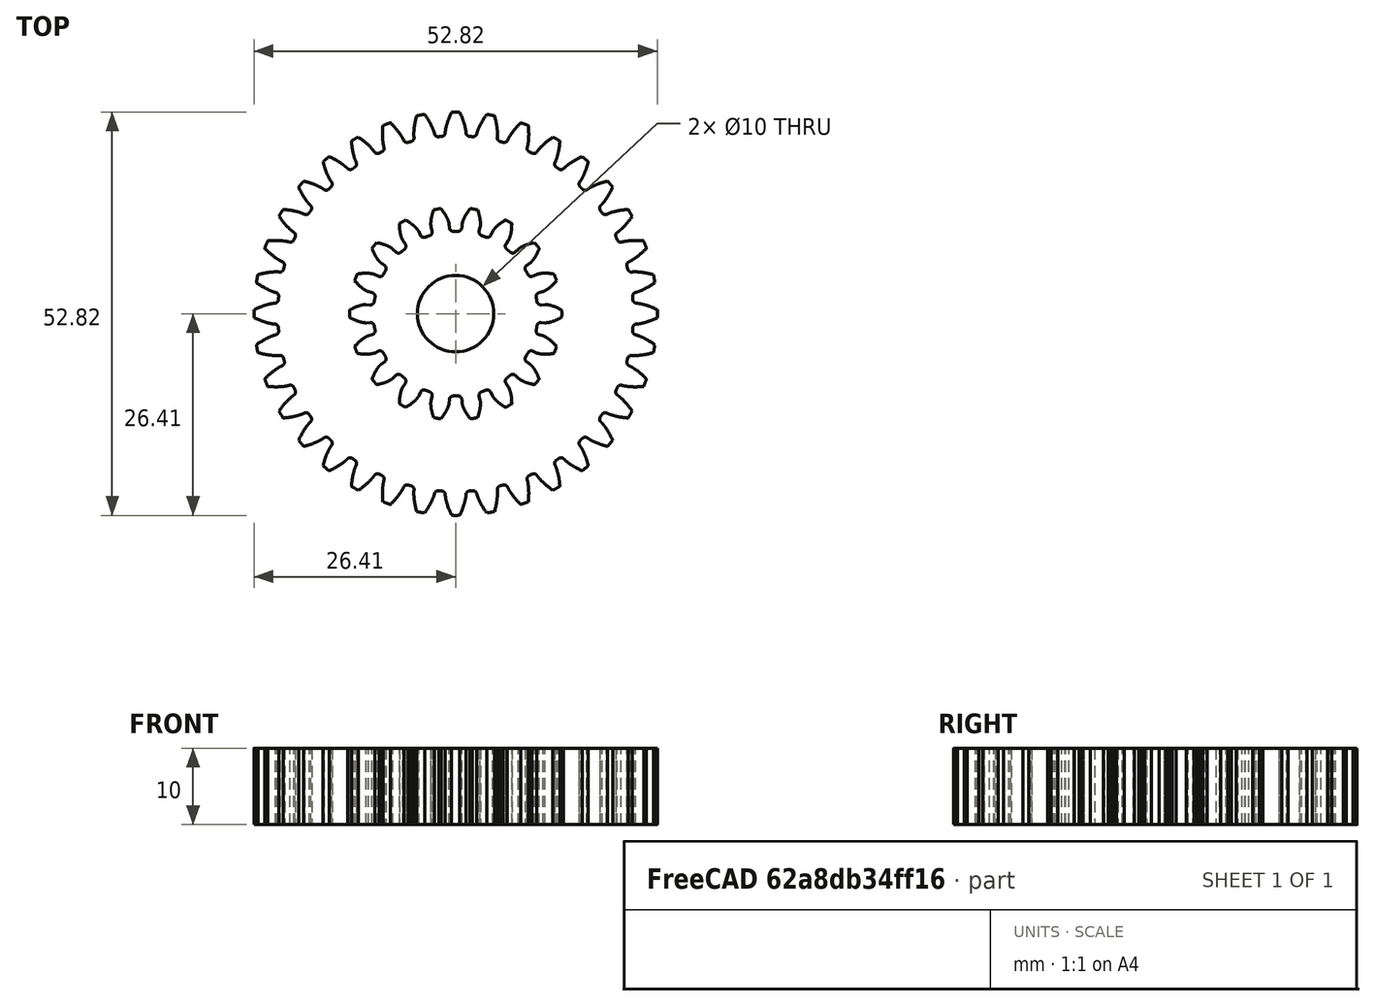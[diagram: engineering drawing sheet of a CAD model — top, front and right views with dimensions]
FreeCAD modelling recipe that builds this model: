
FCSTD DOCUMENT  (FreeCAD 2023.521R36908 (Git))
Label: spur-gear
License: All rights reserved
objects: Part::Part2DObjectPython×2, PartDesign::Pad×2, PartDesign::Body×2, Part::Cylinder×2, Part::Cut×2, App::Part×2
note: 14 computed .brp shape members not serialized (recipe doc carries the construction recipe); baked Part::Feature solids carry a one-line shape summary decoded from their .brp

FEATURE [Part::Part2DObjectPython] InvoluteGear  # Draft 2D object (typed FeaturePython)
  ExternalGear = true
  HighPrecision = true
  InvalidShape = false
  Modules = 1.39
  NumberOfTeeth = 36
  PressureAngle = 20
  TreeRank = 14
  ValidateShape = false
FEATURE [PartDesign::Pad] Pad
  AddSubType = 0
  AlongSketchNormal = false
  AutoTaperInnerAngle = true
  CheckUpToFaceLimits = true
  ClaimChildren = false
  Direction = (0,0,1)
  Fit = 0
  FitJoin = 0
  InnerFit = 0
  InnerFitJoin = 0
  InvalidShape = false
  Length = 10
  Length2 = 10
  Linearize = true
  NewSolid = false
  Profile = -> InvoluteGear
  ReferenceAxis = -> InvoluteGear [N_Axis]
  Suppress = false
  TaperInnerAngle = 0
  TaperInnerAngleRev = 0
  TreeRank = 15
  Type = 0
  ValidateShape = true
  _ProfileBasedVersion = 1
FEATURE [PartDesign::Body] Body
  AutoGroupSolids = false
  ClaimAllChildren = false
  ExportMode = 0
  Group = -> [InvoluteGear,Pad]
  InvalidShape = false
  Origin = -> Origin001
  Tip = -> Pad
  TreeRank = 13
  ValidateShape = false
  _ExportChildren = -> [Pad]
  _GroupVersion = 1
FEATURE [Part::Cylinder] Cylinder
  Angle = 360
  AttacherType = Attacher::AttachEngine3D
  FirstAngle = 0
  Height = 10
  InvalidShape = false
  Radius = 5
  SecondAngle = 0
  TreeRank = 16
  ValidateShape = false
FEATURE [Part::Cut] Cut
  Base = -> Body
  InvalidShape = false
  Tool = -> Cylinder
  TreeRank = 17
  ValidateShape = false
FEATURE [App::Part] Part  label="Gear 1"
  ClaimAllChildren = false
  ExportMode = 1
  Group = -> [Body,Cylinder,Cut]
  Origin = -> Origin
  TreeRank = 3
  _ExportChildren = -> [Cut]
  _GroupVersion = 1
FEATURE [Part::Part2DObjectPython] InvoluteGear001  # Draft 2D object (typed FeaturePython)
  ExternalGear = true
  HighPrecision = true
  InvalidShape = false
  Modules = 1.39
  NumberOfTeeth = 18
  PressureAngle = 20
  TreeRank = 43
  ValidateShape = false
FEATURE [PartDesign::Pad] Pad001
  AddSubType = 0
  AlongSketchNormal = false
  AutoTaperInnerAngle = true
  CheckUpToFaceLimits = true
  ClaimChildren = false
  Direction = (0,0,1)
  Fit = 0
  FitJoin = 0
  InnerFit = 0
  InnerFitJoin = 0
  InvalidShape = false
  Length = 10
  Length2 = 10
  Linearize = true
  NewSolid = false
  Profile = -> InvoluteGear001
  ReferenceAxis = -> InvoluteGear001 [N_Axis]
  Suppress = false
  TaperInnerAngle = 0
  TaperInnerAngleRev = 0
  TreeRank = 44
  Type = 0
  ValidateShape = true
  _ProfileBasedVersion = 1
FEATURE [PartDesign::Body] Body001
  AutoGroupSolids = false
  ClaimAllChildren = false
  ExportMode = 0
  Group = -> [InvoluteGear001,Pad001]
  InvalidShape = false
  Origin = -> Origin003
  Tip = -> Pad001
  TreeRank = 30
  ValidateShape = false
  _ExportChildren = -> [Pad001]
  _GroupVersion = 1
FEATURE [Part::Cylinder] Cylinder001
  Angle = 360
  AttacherType = Attacher::AttachEngine3D
  FirstAngle = 0
  Height = 10
  InvalidShape = false
  Radius = 5
  SecondAngle = 0
  TreeRank = 45
  ValidateShape = false
FEATURE [Part::Cut] Cut001
  Base = -> Body001
  InvalidShape = false
  Tool = -> Cylinder001
  TreeRank = 46
  ValidateShape = false
FEATURE [App::Part] Part001  label="Gear 2"
  ClaimAllChildren = false
  ExportMode = 1
  Group = -> [Body001,Cylinder001,Cut001]
  Origin = -> Origin002
  Placement = pos=(37.53,0,0) rot=(0,0,1;0.174533rad)
  TreeRank = 20
  _ExportChildren = -> [Cut001]
  _GroupVersion = 1
  expr: Placement.Base.x = 1.39 * (36 + 18) / 2
  expr: Placement.Rotation.Angle = 360 / 18 / 2
